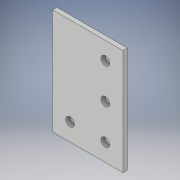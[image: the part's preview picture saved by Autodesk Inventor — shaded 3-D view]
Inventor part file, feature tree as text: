
AUTODESK INVENTOR PART (.ipt)
format: ipt  version: 2017 (Build 210142000, 142)  size: 108,544 bytes
history: native  units: in
note: dims shown in document units (in); Inventor stores cm internally (conversion verified against a paired STEP export)
features: extrude x1, sketch x1
ambient origin geometry x8: Origin, YZ Plane, XZ Plane, XY Plane, X Axis, Y Axis, Z Axis, Center Point
bodies: Solid1 (feature_tree)
feature tree (2):
  extrude  "Extrusion1"  Depth=3.0in
  sketch  "Sketch1"  dims[d0=2.0in d1=3.0in d2=0.25in d3=0.5in d4=0.5in d5=0.25in d6=1.0in d7=0.5in d8=0.25in d9=0.25in d10=0.5in d11=0.5in d12=0.5in d13=1.0in d14=0.125in d15=0.0in]
